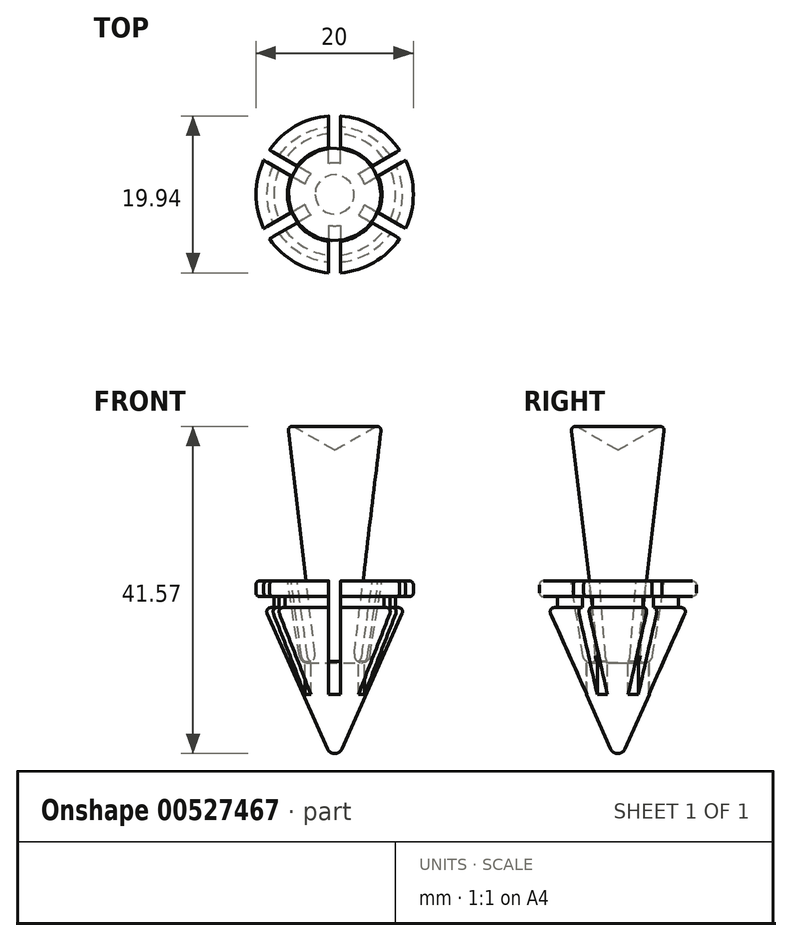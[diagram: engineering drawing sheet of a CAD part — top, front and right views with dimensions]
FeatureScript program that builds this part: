
annotation { "Feature Type Name" : "Feature", "Feature Type Description" : "" }
export const myFeature = defineFeature(function(context is Context, id is Id, definition is map)
    precondition{}
    {
        {
            var Q0;
            Q0=qCreatedBy(makeId("Front.planeOp"),FACE);
            var sketch = newSketch(context, id + "F0", { "sketchPlane" : qUnion([Q0])});
            skLineSegment(sketch, "E0", {"start": v(0, 1.46) * mm, "end": v(0, 40) * mm});
            skLineSegment(sketch, "E1", {"start": v(0, 40) * mm, "end": v(-6, 43.46) * mm});
            skLineSegment(sketch, "E2", {"start": v(-7.73, 20) * mm, "end": v(-8.12, 20) * mm});
            skLineSegment(sketch, "E3", {"start": v(-8.58, 19.3) * mm, "end": v(-0.91, 2.05) * mm});
            skLineSegment(sketch, "E4", {"start": v(-7.62, 23.56) * mm, "end": v(-7.62, 0) * mm, "construction": true});
            skArc(sketch, "E5", {"start": v(-0.91, 2.05) * mm, "mid": v(-0.54, 1.62) * mm, "end": v(0, 1.46) * mm});
            skPoint(sketch, "E6.orphan", {"position": v(0, 0) * mm});
            skPoint(sketch, "E7.visualSharp", {"position": v(-8.9, 20) * mm});
            skArc(sketch, "E7.filletArc", {"start": v(-8.12, 20) * mm, "mid": v(-8.54, 19.77) * mm, "end": v(-8.58, 19.3) * mm});
            skLineSegment(sketch, "E8", {"start": v(-7.73, 20) * mm, "end": v(-7.73, 21.4) * mm});
            skLineSegment(sketch, "E9", {"start": v(-7.73, 21.4) * mm, "end": v(-10, 21.4) * mm});
            skLineSegment(sketch, "E10", {"start": v(-10, 21.4) * mm, "end": v(-10, 23.4) * mm});
            skLineSegment(sketch, "E11", {"start": v(-10, 23.4) * mm, "end": v(-6, 23.4) * mm});
            skArc(sketch, "E12.filletArc", {"start": v(-4.48, 13.85) * mm, "mid": v(-3.36, 13.02) * mm, "end": v(-2.5, 14.12) * mm});
            skLineSegment(sketch, "E13", {"start": v(-2.5, 14.12) * mm, "end": v(-6, 43.46) * mm});
            skLineSegment(sketch, "E14", {"start": v(-6, 23.4) * mm, "end": v(-4.48, 13.85) * mm});
            skSolve(sketch);
        }
        {
            var Q0;
            Q0=makeQuery(id+"F0.imprint","IMPRINT",FACE,{"disambiguationData":[TD([[makeQuery(id+"F0.imprint","IMPRINT",EDGE,{"derivedFrom":sQuery(id+"F0.wireOp",EDGE,"E0")}),1.0]])]});
            var Q1;
            Q1=sQuery(id+"F0.wireOp",EDGE,"E0");
            revolve(context, id + "F1", {"entities" : qUnion([Q0]), "axis" : qUnion([Q1]), "revolveType" : RevolveType.FULL});
        }
        {
            var Q0;
            Q0=makeQuery(id+"F1.opRevolve","SWEPT_EDGE",EDGE,{"disambiguationData":[OSD([sQuery(id+"F0.wireOp",EDGE,"E10"),sQuery(id+"F0.wireOp",EDGE,"E11")])]});
            var Q1;
            Q1=makeQuery(id+"F1.opRevolve","SWEPT_EDGE",EDGE,{"disambiguationData":[OSD([sQuery(id+"F0.wireOp",EDGE,"E9"),sQuery(id+"F0.wireOp",EDGE,"E10")])]});
            var Q2;
            Q2=makeQuery(id+"F1.opRevolve","SWEPT_EDGE",EDGE,{"disambiguationData":[OSD([sQuery(id+"F0.wireOp",EDGE,"E1"),sQuery(id+"F0.wireOp",EDGE,"E13")])]});
            fillet(context, id + "F2", {"entities" : qUnion([Q0, Q1, Q2]), "radius" : 0.5 * mm, "tangentPropagation" : true, "allowEdgeOverflow" : false});
        }
        {
            var Q0;
            Q0=qCreatedBy(makeId("Top.planeOp"),FACE);
            var sketch = newSketch(context, id + "F3", { "sketchPlane" : qUnion([Q0])});
            skLineSegment(sketch, "E15", {"start": v(0, 0) * mm, "end": v(0, 18.4) * mm, "construction": true});
            skLineSegment(sketch, "E16.top", {"start": v(0.75, 10.71) * mm, "end": v(-0.75, 10.71) * mm});
            skLineSegment(sketch, "E16.left", {"start": v(0.75, 3.93) * mm, "end": v(0.75, 10.71) * mm});
            skLineSegment(sketch, "E16.right", {"start": v(-0.75, 3.93) * mm, "end": v(-0.75, 10.71) * mm});
            skPoint(sketch, "E16.middle", {"position": v(0, 7.32) * mm});
            skArc(sketch, "E17.0", {"start": v(0.75, 3.93) * mm, "mid": v(0, 4) * mm, "end": v(-0.75, 3.93) * mm});
            skLineSegment(sketch, "E18.1.0", {"start": v(-3.03, 2.61) * mm, "end": v(-8.9, 6) * mm});
            skLineSegment(sketch, "E18.1.1", {"start": v(-3.78, 1.32) * mm, "end": v(-9.65, 4.7) * mm});
            skArc(sketch, "E18.1.2", {"start": v(-3.03, 2.61) * mm, "mid": v(-3.46, 2) * mm, "end": v(-3.78, 1.32) * mm});
            skPoint(sketch, "E18.1.3", {"position": v(-6.34, 3.66) * mm});
            skLineSegment(sketch, "E18.1.4", {"start": v(-8.9, 6) * mm, "end": v(-9.65, 4.7) * mm});
            skLineSegment(sketch, "E18.2.0", {"start": v(-3.78, -1.32) * mm, "end": v(-9.65, -4.7) * mm});
            skLineSegment(sketch, "E18.2.1", {"start": v(-3.03, -2.61) * mm, "end": v(-8.9, -6) * mm});
            skArc(sketch, "E18.2.2", {"start": v(-3.78, -1.32) * mm, "mid": v(-3.46, -2) * mm, "end": v(-3.03, -2.61) * mm});
            skPoint(sketch, "E18.2.3", {"position": v(-6.34, -3.66) * mm});
            skLineSegment(sketch, "E18.2.4", {"start": v(-9.65, -4.7) * mm, "end": v(-8.9, -6) * mm});
            skLineSegment(sketch, "E19.3.3.0", {"start": v(0.75, -3.93) * mm, "end": v(0.75, -10.71) * mm});
            skLineSegment(sketch, "E19.4.3.0", {"start": v(-0.75, -3.93) * mm, "end": v(-0.75, -10.71) * mm});
            skArc(sketch, "E19.6.3.0", {"start": v(-0.75, -3.93) * mm, "mid": v(0, -4) * mm, "end": v(0.75, -3.93) * mm});
            skPoint(sketch, "E19.10.3.0", {"position": v(0, -7.32) * mm});
            skLineSegment(sketch, "E19.11.3.0", {"start": v(-0.75, -10.71) * mm, "end": v(0.75, -10.71) * mm});
            skLineSegment(sketch, "E19.3.4.0", {"start": v(3.78, -1.32) * mm, "end": v(9.65, -4.7) * mm});
            skLineSegment(sketch, "E19.4.4.0", {"start": v(3.03, -2.61) * mm, "end": v(8.9, -6) * mm});
            skArc(sketch, "E19.6.4.0", {"start": v(3.03, -2.61) * mm, "mid": v(3.46, -2) * mm, "end": v(3.78, -1.32) * mm});
            skPoint(sketch, "E19.10.4.0", {"position": v(6.34, -3.66) * mm});
            skLineSegment(sketch, "E19.11.4.0", {"start": v(8.9, -6) * mm, "end": v(9.65, -4.7) * mm});
            skLineSegment(sketch, "E19.3.5.0", {"start": v(3.03, 2.61) * mm, "end": v(8.9, 6) * mm});
            skLineSegment(sketch, "E19.4.5.0", {"start": v(3.78, 1.32) * mm, "end": v(9.65, 4.7) * mm});
            skArc(sketch, "E19.6.5.0", {"start": v(3.78, 1.32) * mm, "mid": v(3.46, 2) * mm, "end": v(3.03, 2.61) * mm});
            skPoint(sketch, "E19.10.5.0", {"position": v(6.34, 3.66) * mm});
            skLineSegment(sketch, "E19.11.5.0", {"start": v(9.65, 4.7) * mm, "end": v(8.9, 6) * mm});
            skSolve(sketch);
        }
        {
            var Q0;
            Q0 = qSketchRegion(id + "F3", true);
            extrude(context, id + "F4", {"entities" : qUnion([Q0]), "operationType" : NewBodyOperationType.REMOVE, "oppositeDirection" : true, "depth" : 25 * mm, "offsetDistance" : 25 * mm, "hasSecondDirection" : true, "secondDirectionOppositeDirection" : false, "secondDirectionDepth" : 25 * mm});
        }
    });
